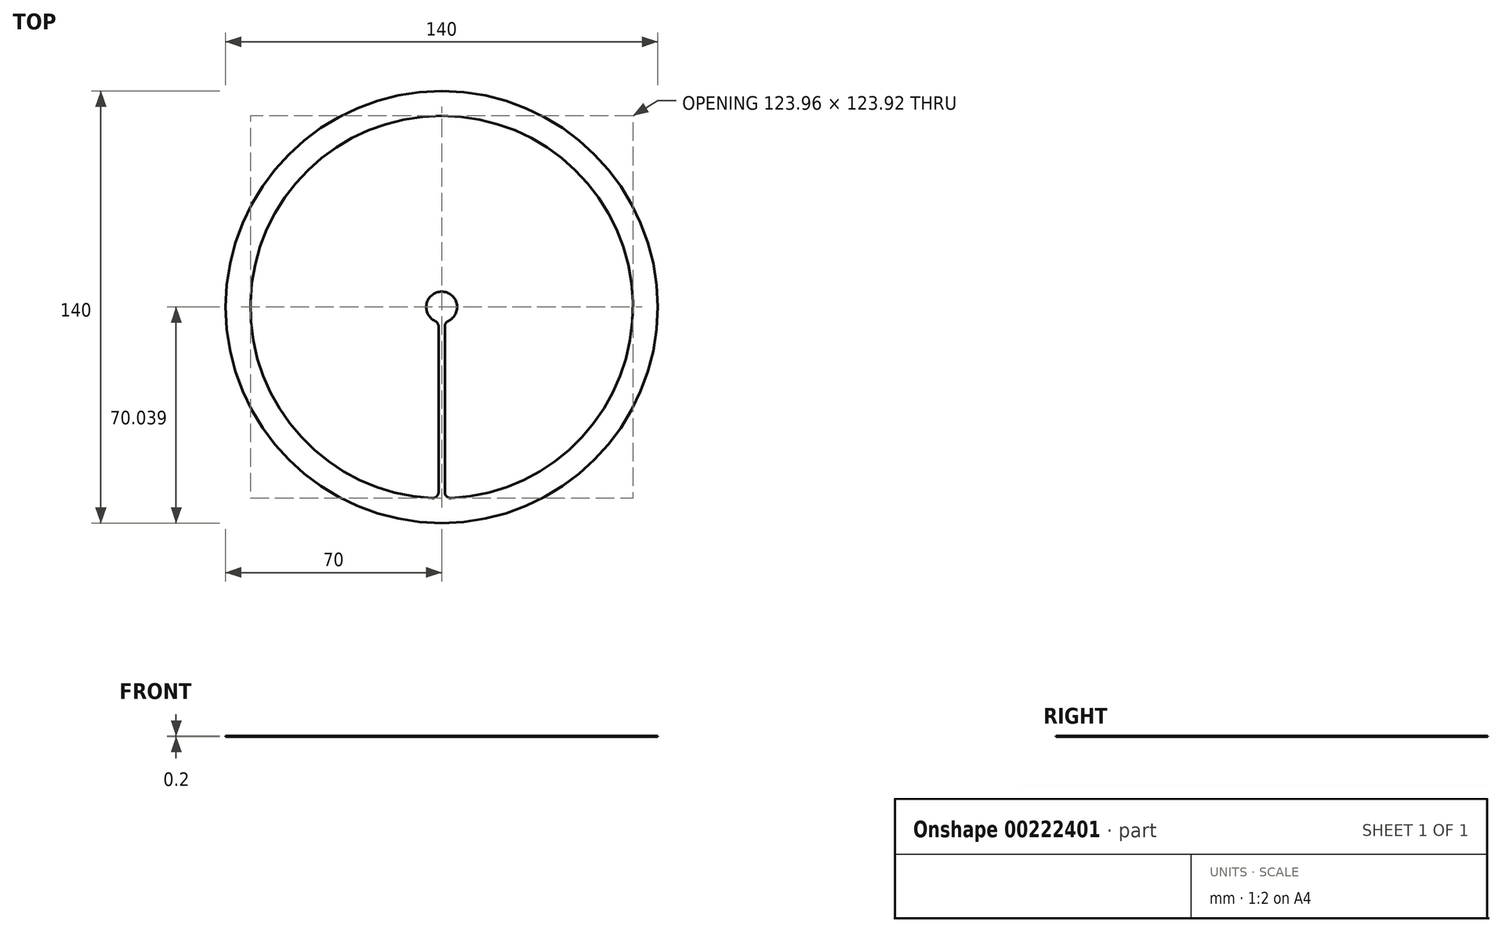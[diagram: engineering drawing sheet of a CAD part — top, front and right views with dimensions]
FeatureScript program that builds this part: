
annotation { "Feature Type Name" : "Feature", "Feature Type Description" : "" }
export const myFeature = defineFeature(function(context is Context, id is Id, definition is map)
    precondition{}
    {
        {
            var Q0;
            Q0=qCreatedBy(makeId("Top.planeOp"),FACE);
            var sketch = newSketch(context, id + "F0", { "sketchPlane" : qUnion([Q0])});
            skCircle(sketch, "E0", {"center": v(0, 0) * mm, "radius": 70 * mm});
            skArc(sketch, "E1", {"start": v(1, -62) * mm, "mid": v(0, 62) * mm, "end": v(-1, -62) * mm});
            skArc(sketch, "E2", {"start": v(1, -4.9) * mm, "mid": v(0, 5) * mm, "end": v(-1, -4.9) * mm});
            skLineSegment(sketch, "E3.left", {"start": v(-1, -62) * mm, "end": v(-1, -4.9) * mm});
            skLineSegment(sketch, "E3.right", {"start": v(1, -62) * mm, "end": v(1, -4.9) * mm});
            skSolve(sketch);
        }
        {
            var Q0;
            Q0 = qSketchRegion(id + "F0", true);
            var Q1;
            Q1=makeQuery(id+"F0.imprint","IMPRINT",FACE,{"disambiguationData":[TD([[makeQuery(id+"F0.imprint","IMPRINT",EDGE,{"derivedFrom":sQuery(id+"F0.wireOp",EDGE,"E2")}),1.0]])]});
            extrude(context, id + "F1", {"entities" : qUnion([Q0, Q1]), "depth" : 0.2 * mm});
        }
        {
            var Q0;
            Q0=makeQuery(id+"F1.opExtrude","SWEPT_EDGE",EDGE,{"disambiguationData":[OSD([sQuery(id+"F0.wireOp",EDGE,"E2"),sQuery(id+"F0.wireOp",EDGE,"E3.right")])]});
            var Q1;
            Q1=makeQuery(id+"F1.opExtrude","SWEPT_EDGE",EDGE,{"disambiguationData":[OSD([sQuery(id+"F0.wireOp",EDGE,"E2"),sQuery(id+"F0.wireOp",EDGE,"E3.left")])]});
            var Q2;
            Q2=makeQuery(id+"F1.opExtrude","SWEPT_EDGE",EDGE,{"disambiguationData":[OSD([sQuery(id+"F0.wireOp",EDGE,"E1"),sQuery(id+"F0.wireOp",EDGE,"E3.right")])]});
            var Q3;
            Q3=makeQuery(id+"F1.opExtrude","SWEPT_EDGE",EDGE,{"disambiguationData":[OSD([sQuery(id+"F0.wireOp",EDGE,"E1"),sQuery(id+"F0.wireOp",EDGE,"E3.left")])]});
            fillet(context, id + "F2", {"entities" : qUnion([Q0, Q1, Q2, Q3]), "radius" : 2 * mm, "tangentPropagation" : true, "allowEdgeOverflow" : false});
        }
    });
